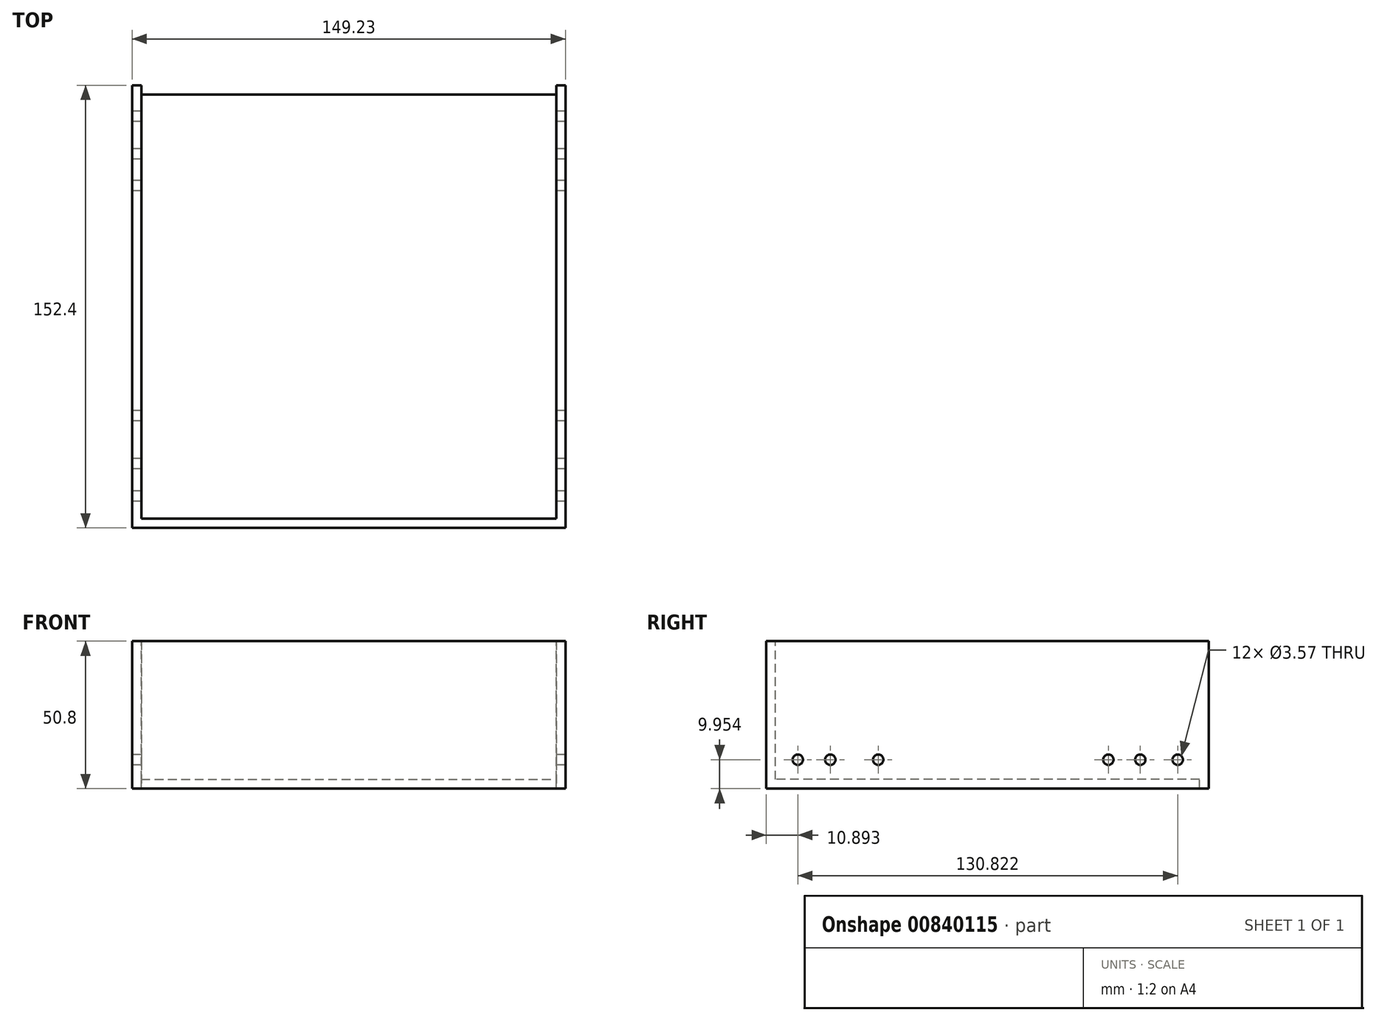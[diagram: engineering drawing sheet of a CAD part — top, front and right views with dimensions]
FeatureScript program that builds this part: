
annotation { "Feature Type Name" : "Feature", "Feature Type Description" : "" }
export const myFeature = defineFeature(function(context is Context, id is Id, definition is map)
    precondition{}
    {
        {
            var Q0;
            Q0=qCreatedBy(makeId("Top.planeOp"),FACE);
            var sketch = newSketch(context, id + "F0", { "sketchPlane" : qUnion([Q0])});
            skLineSegment(sketch, "E0.bottom", {"start": v(0, 0) * mm, "end": v(152.4, 0) * mm});
            skLineSegment(sketch, "E0.top", {"start": v(0, 152.4) * mm, "end": v(152.4, 152.4) * mm});
            skLineSegment(sketch, "E0.left", {"start": v(0, 0) * mm, "end": v(0, 152.4) * mm});
            skLineSegment(sketch, "E0.right", {"start": v(152.4, 0) * mm, "end": v(152.4, 152.4) * mm});
            skLineSegment(sketch, "E1.top", {"start": v(0, 3.18) * mm, "end": v(152.4, 3.18) * mm});
            skLineSegment(sketch, "E1.left", {"start": v(0, 0) * mm, "end": v(0, 3.18) * mm});
            skLineSegment(sketch, "E1.right", {"start": v(152.4, 0) * mm, "end": v(152.4, 3.17) * mm});
            skLineSegment(sketch, "E2.bottom", {"start": v(152.4, 0) * mm, "end": v(149.23, 0) * mm});
            skLineSegment(sketch, "E2.top", {"start": v(152.4, 152.4) * mm, "end": v(149.22, 152.4) * mm});
            skLineSegment(sketch, "E2.right", {"start": v(149.23, 0) * mm, "end": v(149.22, 152.4) * mm});
            skLineSegment(sketch, "E3.top", {"start": v(0, 149.22) * mm, "end": v(152.4, 149.22) * mm});
            skLineSegment(sketch, "E3.left", {"start": v(0, 152.4) * mm, "end": v(0, 149.22) * mm});
            skLineSegment(sketch, "E3.right", {"start": v(152.4, 152.4) * mm, "end": v(152.4, 149.22) * mm});
            skSolve(sketch);
        }
        {
            var Q0;
            {var subQ0=sQuery(id+"F0.wireOp",EDGE,"E0.left");var subQ1=sQuery(id+"F0.wireOp",EDGE,"E0.bottom");var subQ2=makeQuery(id+"F0.imprint","INTERSECT",VERTEX,{"derivedFrom":[subQ1,subQ0]});Q0=makeQuery(id+"F0.imprint","IMPRINT",FACE,{"disambiguationData":[TD([[makeQuery(id+"F0.imprint","IMPRINT",EDGE,{"disambiguationData":[TD([[subQ2,-1.0]])],"derivedFrom":subQ1}),1.0]])]});}
            extrude(context, id + "F1", {"entities" : qUnion([Q0]), "depth" : 50.8 * mm, "offsetDistance" : 25.4 * mm});
        }
        {
            var Q0;
            {var subQ0=sQuery(id+"F0.wireOp",EDGE,"E1.top");var subQ1=sQuery(id+"F0.wireOp",EDGE,"E0.left");var subQ2=makeQuery(id+"F0.imprint","INTERSECT",VERTEX,{"derivedFrom":[subQ1,subQ0]});Q0=makeQuery(id+"F0.imprint","IMPRINT",FACE,{"disambiguationData":[TD([[makeQuery(id+"F0.imprint","IMPRINT",EDGE,{"disambiguationData":[TD([[subQ2,-1.0]])],"derivedFrom":subQ1}),-1.0]])]});}
            extrude(context, id + "F2", {"entities" : qUnion([Q0]), "operationType" : NewBodyOperationType.ADD, "depth" : 3.17 * mm, "offsetDistance" : 25.4 * mm});
        }
        {
            var Q0;
            Q0=qCreatedBy(makeId("Top.planeOp"),FACE);
            var sketch = newSketch(context, id + "F3", { "sketchPlane" : qUnion([Q0])});
            skLineSegment(sketch, "E4.bottom", {"start": v(0, 0) * mm, "end": v(3.18, 0) * mm});
            skLineSegment(sketch, "E4.top", {"start": v(0, 152.4) * mm, "end": v(3.17, 152.4) * mm});
            skLineSegment(sketch, "E4.left", {"start": v(0, 0) * mm, "end": v(0, 152.4) * mm});
            skLineSegment(sketch, "E4.right", {"start": v(3.18, 0) * mm, "end": v(3.17, 152.4) * mm});
            skSolve(sketch);
        }
        {
            var Q0;
            Q0 = qSketchRegion(id + "F3", true);
            extrude(context, id + "F4", {"entities" : qUnion([Q0]), "operationType" : NewBodyOperationType.ADD, "depth" : 50.8 * mm, "offsetDistance" : 25.4 * mm});
        }
        {
            var Q0;
            Q0=qCreatedBy(makeId("Top.planeOp"),FACE);
            var sketch = newSketch(context, id + "F5", { "sketchPlane" : qUnion([Q0])});
            skLineSegment(sketch, "E5.bottom", {"start": v(149.23, 0) * mm, "end": v(146.05, 0) * mm});
            skLineSegment(sketch, "E5.top", {"start": v(149.22, 152.4) * mm, "end": v(146.05, 152.4) * mm});
            skLineSegment(sketch, "E5.left", {"start": v(149.23, 0) * mm, "end": v(149.22, 152.4) * mm});
            skLineSegment(sketch, "E5.right", {"start": v(146.05, 0) * mm, "end": v(146.05, 152.4) * mm});
            skSolve(sketch);
        }
        {
            var Q0;
            Q0=makeQuery(id+"F5.imprint","IMPRINT",FACE,{"disambiguationData":[TD([[makeQuery(id+"F5.imprint","IMPRINT",EDGE,{"derivedFrom":sQuery(id+"F5.wireOp",EDGE,"E5.bottom")}),-1.0]])]});
            extrude(context, id + "F6", {"entities" : qUnion([Q0]), "operationType" : NewBodyOperationType.ADD, "depth" : 50.8 * mm, "offsetDistance" : 25.4 * mm});
        }
        {
            var Q0;
            Q0=qCreatedBy(makeId("Right.planeOp"),FACE);
            var sketch = newSketch(context, id + "F7", { "sketchPlane" : qUnion([Q0])});
            skCircle(sketch, "E6", {"center": v(10.9, 9.95) * mm, "radius": 1.79 * mm});
            skCircle(sketch, "E7", {"center": v(22.08, 9.95) * mm, "radius": 1.79 * mm});
            skCircle(sketch, "E8", {"center": v(38.57, 9.95) * mm, "radius": 1.79 * mm});
            skCircle(sketch, "E9", {"center": v(141.71, 9.95) * mm, "radius": 1.79 * mm});
            skCircle(sketch, "E10", {"center": v(128.82, 9.95) * mm, "radius": 1.79 * mm});
            skCircle(sketch, "E11", {"center": v(117.83, 9.95) * mm, "radius": 1.79 * mm});
            skSolve(sketch);
        }
        {
            var Q0;
            Q0 = qSketchRegion(id + "F7", true);
            extrude(context, id + "F8", {"entities" : qUnion([Q0]), "operationType" : NewBodyOperationType.REMOVE, "depth" : 254 * mm, "offsetDistance" : 25.4 * mm});
        }
    });
